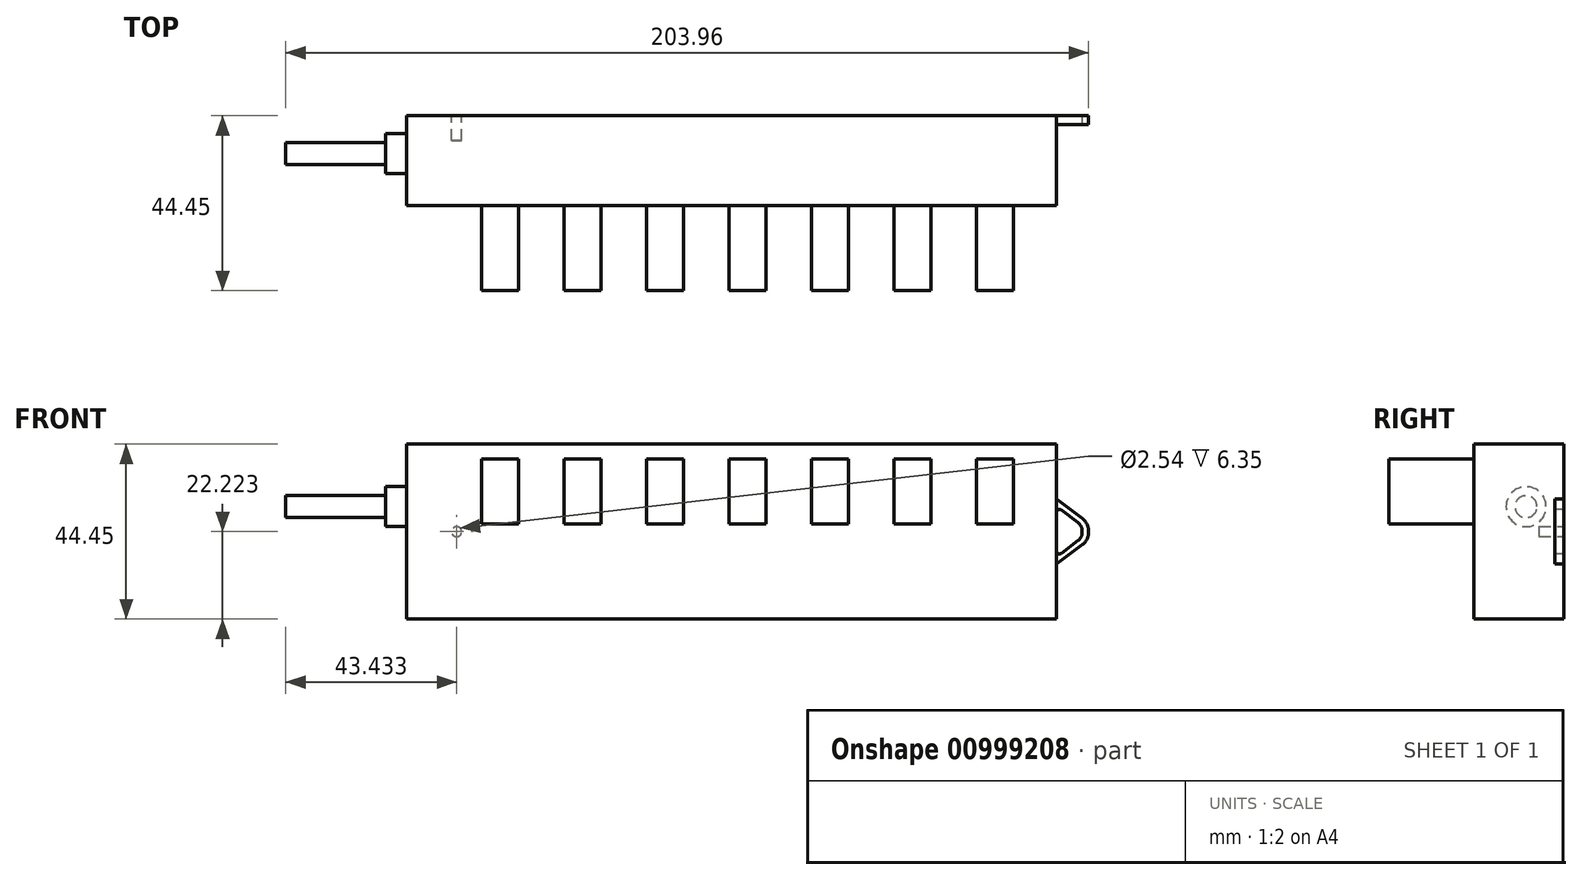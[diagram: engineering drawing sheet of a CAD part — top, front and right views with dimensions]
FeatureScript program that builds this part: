
annotation { "Feature Type Name" : "Feature", "Feature Type Description" : "" }
export const myFeature = defineFeature(function(context is Context, id is Id, definition is map)
    precondition{}
    {
        {
            var Q0;
            Q0=qCreatedBy(makeId("Front.planeOp"),FACE);
            var sketch = newSketch(context, id + "F0", { "sketchPlane" : qUnion([Q0])});
            skLineSegment(sketch, "E0.bottom", {"start": v(-60.25, 51.98) * mm, "end": v(104.85, 51.98) * mm});
            skLineSegment(sketch, "E0.top", {"start": v(-60.25, 7.53) * mm, "end": v(104.85, 7.53) * mm});
            skLineSegment(sketch, "E0.left", {"start": v(-60.25, 51.98) * mm, "end": v(-60.25, 7.53) * mm});
            skLineSegment(sketch, "E0.right", {"start": v(104.85, 51.98) * mm, "end": v(104.85, 7.53) * mm});
            skSolve(sketch);
        }
        {
            var Q0;
            Q0=makeQuery(id+"F0.imprint","IMPRINT",FACE,{"disambiguationData":[TD([[makeQuery(id+"F0.imprint","IMPRINT",EDGE,{"derivedFrom":sQuery(id+"F0.wireOp",EDGE,"E0.bottom")}),-1.0]])]});
            extrude(context, id + "F1", {"entities" : qUnion([Q0]), "depth" : 22.86 * mm, "offsetDistance" : 25.4 * mm});
        }
        {
            var Q0;
            Q0=makeQuery(id+"F1.opExtrude","SWEPT_FACE",FACE,{"disambiguationData":[OSD([sQuery(id+"F0.wireOp",EDGE,"E0.left")])]});
            var sketch = newSketch(context, id + "F2", { "sketchPlane" : qUnion([Q0])});
            skCircle(sketch, "E1", {"center": v(9.65, 36.1) * mm, "radius": 5.08 * mm});
            skSolve(sketch);
        }
        {
            var Q0;
            Q0 = qSketchRegion(id + "F2", true);
            extrude(context, id + "F3", {"entities" : qUnion([Q0]), "operationType" : NewBodyOperationType.ADD, "depth" : 5.33 * mm, "offsetDistance" : 25.4 * mm});
        }
        {
            var Q0;
            Q0=makeQuery(id+"F3.opExtrude","CAP_FACE",FACE,{"disambiguationData":[OSD([sQuery(id+"F2.wireOp",EDGE,"E1")])],"isStart":false});
            var sketch = newSketch(context, id + "F4", { "sketchPlane" : qUnion([Q0])});
            skCircle(sketch, "E2", {"center": v(9.65, 36.1) * mm, "radius": 2.8 * mm});
            skSolve(sketch);
        }
        {
            var Q0;
            Q0 = qSketchRegion(id + "F4", true);
            extrude(context, id + "F5", {"entities" : qUnion([Q0]), "operationType" : NewBodyOperationType.ADD, "depth" : 25.4 * mm, "offsetDistance" : 25.4 * mm});
        }
        {
            var Q0;
            Q0=makeQuery(id+"F1.opExtrude","CAP_FACE",FACE,{"disambiguationData":[OSD([sQuery(id+"F0.wireOp",EDGE,"E0.bottom"),sQuery(id+"F0.wireOp",EDGE,"E0.top"),sQuery(id+"F0.wireOp",EDGE,"E0.left"),sQuery(id+"F0.wireOp",EDGE,"E0.right")])],"isStart":false});
            var sketch = newSketch(context, id + "F6", { "sketchPlane" : qUnion([Q0])});
            skLineSegment(sketch, "E3.bottom", {"start": v(-41.2, 48.17) * mm, "end": v(-31.8, 48.17) * mm});
            skLineSegment(sketch, "E3.top", {"start": v(-41.2, 31.66) * mm, "end": v(-31.8, 31.66) * mm});
            skLineSegment(sketch, "E3.left", {"start": v(-41.2, 48.17) * mm, "end": v(-41.2, 31.66) * mm});
            skLineSegment(sketch, "E3.right", {"start": v(-31.8, 48.17) * mm, "end": v(-31.8, 31.66) * mm});
            skLineSegment(sketch, "E4.1.0.0", {"start": v(-10.84, 48.17) * mm, "end": v(-10.84, 31.66) * mm});
            skLineSegment(sketch, "E4.1.0.1", {"start": v(-20.24, 48.17) * mm, "end": v(-10.84, 48.17) * mm});
            skLineSegment(sketch, "E4.1.0.2", {"start": v(-20.24, 48.17) * mm, "end": v(-20.24, 31.66) * mm});
            skLineSegment(sketch, "E4.1.0.3", {"start": v(-20.24, 31.66) * mm, "end": v(-10.84, 31.66) * mm});
            skLineSegment(sketch, "E4.2.0.0", {"start": v(10.11, 48.17) * mm, "end": v(10.11, 31.66) * mm});
            skLineSegment(sketch, "E4.2.0.1", {"start": v(0.71, 48.17) * mm, "end": v(10.11, 48.17) * mm});
            skLineSegment(sketch, "E4.2.0.2", {"start": v(0.71, 48.17) * mm, "end": v(0.71, 31.66) * mm});
            skLineSegment(sketch, "E4.2.0.3", {"start": v(0.71, 31.66) * mm, "end": v(10.11, 31.66) * mm});
            skLineSegment(sketch, "E4.3.0.0", {"start": v(31.07, 48.17) * mm, "end": v(31.07, 31.66) * mm});
            skLineSegment(sketch, "E4.3.0.1", {"start": v(21.67, 48.17) * mm, "end": v(31.07, 48.17) * mm});
            skLineSegment(sketch, "E4.3.0.2", {"start": v(21.67, 48.17) * mm, "end": v(21.67, 31.66) * mm});
            skLineSegment(sketch, "E4.3.0.3", {"start": v(21.67, 31.66) * mm, "end": v(31.07, 31.66) * mm});
            skLineSegment(sketch, "E4.4.0.0", {"start": v(52.02, 48.17) * mm, "end": v(52.02, 31.66) * mm});
            skLineSegment(sketch, "E4.4.0.1", {"start": v(42.62, 48.17) * mm, "end": v(52.02, 48.17) * mm});
            skLineSegment(sketch, "E4.4.0.2", {"start": v(42.62, 48.17) * mm, "end": v(42.62, 31.66) * mm});
            skLineSegment(sketch, "E4.4.0.3", {"start": v(42.62, 31.66) * mm, "end": v(52.02, 31.66) * mm});
            skLineSegment(sketch, "E4.5.0.0", {"start": v(72.98, 48.17) * mm, "end": v(72.98, 31.66) * mm});
            skLineSegment(sketch, "E4.5.0.1", {"start": v(63.58, 48.17) * mm, "end": v(72.98, 48.17) * mm});
            skLineSegment(sketch, "E4.5.0.2", {"start": v(63.58, 48.17) * mm, "end": v(63.58, 31.66) * mm});
            skLineSegment(sketch, "E4.5.0.3", {"start": v(63.58, 31.66) * mm, "end": v(72.98, 31.66) * mm});
            skLineSegment(sketch, "E4.6.0.0", {"start": v(93.93, 48.17) * mm, "end": v(93.93, 31.66) * mm});
            skLineSegment(sketch, "E4.6.0.1", {"start": v(84.53, 48.17) * mm, "end": v(93.93, 48.17) * mm});
            skLineSegment(sketch, "E4.6.0.2", {"start": v(84.53, 48.17) * mm, "end": v(84.53, 31.66) * mm});
            skLineSegment(sketch, "E4.6.0.3", {"start": v(84.53, 31.66) * mm, "end": v(93.93, 31.66) * mm});
            skLineSegment(sketch, "E4.direction1", {"start": v(-31.8, 31.66) * mm, "end": v(-10.84, 31.66) * mm, "construction": true});
            skSolve(sketch);
        }
        {
            var Q0;
            Q0 = qSketchRegion(id + "F6", true);
            extrude(context, id + "F7", {"entities" : qUnion([Q0]), "operationType" : NewBodyOperationType.ADD, "depth" : 21.59 * mm, "offsetDistance" : 25.4 * mm});
        }
        {
            var Q0;
            Q0=makeQuery(id+"F1.opExtrude","SWEPT_FACE",FACE,{"disambiguationData":[OSD([sQuery(id+"F0.wireOp",EDGE,"E0.right")])]});
            var sketch = newSketch(context, id + "F8", { "sketchPlane" : qUnion([Q0])});
            skLineSegment(sketch, "E5.bottom", {"start": v(0, 38) * mm, "end": v(-2.29, 38) * mm});
            skLineSegment(sketch, "E5.top", {"start": v(0, 21.5) * mm, "end": v(-2.29, 21.5) * mm});
            skLineSegment(sketch, "E5.left", {"start": v(0, 38) * mm, "end": v(0, 21.5) * mm});
            skLineSegment(sketch, "E5.right", {"start": v(-2.29, 38) * mm, "end": v(-2.29, 21.5) * mm});
            skSolve(sketch);
        }
        {
            var Q0;
            Q0 = qSketchRegion(id + "F8", true);
            extrude(context, id + "F9", {"entities" : qUnion([Q0]), "operationType" : NewBodyOperationType.ADD, "depth" : 8.13 * mm, "offsetDistance" : 25.4 * mm});
        }
        {
            var Q0;
            Q0=makeQuery(id+"F9.opExtrude","SWEPT_FACE",FACE,{"disambiguationData":[OSD([sQuery(id+"F8.wireOp",EDGE,"E5.right")])]});
            var sketch = newSketch(context, id + "F10", { "sketchPlane" : qUnion([Q0])});
            skLineSegment(sketch, "E6", {"start": v(104.85, 38) * mm, "end": v(111.46, 33.06) * mm});
            skLineSegment(sketch, "E7", {"start": v(104.85, 38) * mm, "end": v(112.98, 38) * mm});
            skLineSegment(sketch, "E8", {"start": v(112.98, 38) * mm, "end": v(112.98, 31.91) * mm});
            skLineSegment(sketch, "E9", {"start": v(104.85, 29.75) * mm, "end": v(112.98, 29.75) * mm, "construction": true});
            skLineSegment(sketch, "E10", {"start": v(106.07, 35.24) * mm, "end": v(110.34, 32.04) * mm});
            skLineSegment(sketch, "E11", {"start": v(111.36, 30) * mm, "end": v(111.36, 29.75) * mm});
            skPoint(sketch, "E12.visualSharp", {"position": v(111.36, 31.28) * mm});
            skArc(sketch, "E12.filletArc", {"start": v(111.36, 30) * mm, "mid": v(111.09, 31.14) * mm, "end": v(110.34, 32.04) * mm});
            skLineSegment(sketch, "E13", {"start": v(112.98, 30) * mm, "end": v(112.98, 29.75) * mm});
            skPoint(sketch, "E14.visualSharp", {"position": v(112.98, 31.91) * mm});
            skArc(sketch, "E14.filletArc", {"start": v(112.98, 30) * mm, "mid": v(112.58, 31.71) * mm, "end": v(111.46, 33.06) * mm});
            skLineSegment(sketch, "E15", {"start": v(104.85, 34.63) * mm, "end": v(104.85, 29.75) * mm});
            skPoint(sketch, "E16.visualSharp", {"position": v(104.85, 36.15) * mm});
            skArc(sketch, "E16.filletArc", {"start": v(106.07, 35.24) * mm, "mid": v(105.27, 35.31) * mm, "end": v(104.85, 34.63) * mm});
            skLineSegment(sketch, "E17", {"start": v(111.36, 29.75) * mm, "end": v(104.85, 29.75) * mm});
            skLineSegment(sketch, "E18", {"start": v(112.98, 31.91) * mm, "end": v(112.98, 29.75) * mm});
            skLineSegment(sketch, "E19.MirrorCS", {"start": v(104.85, 24.88) * mm, "end": v(104.85, 29.75) * mm});
            skArc(sketch, "E20.MirrorCS", {"start": v(106.07, 24.27) * mm, "mid": v(105.27, 24.2) * mm, "end": v(104.85, 24.88) * mm});
            skLineSegment(sketch, "E21.MirrorCS", {"start": v(106.07, 24.27) * mm, "end": v(110.34, 27.47) * mm});
            skArc(sketch, "E22.MirrorCS", {"start": v(111.36, 29.5) * mm, "mid": v(111.09, 28.36) * mm, "end": v(110.34, 27.47) * mm});
            skLineSegment(sketch, "E23.MirrorCS", {"start": v(111.36, 29.5) * mm, "end": v(111.36, 29.75) * mm});
            skLineSegment(sketch, "E24.MirrorCS", {"start": v(112.98, 29.5) * mm, "end": v(112.98, 29.75) * mm});
            skArc(sketch, "E25.MirrorCS", {"start": v(112.98, 29.5) * mm, "mid": v(112.58, 27.8) * mm, "end": v(111.46, 26.45) * mm});
            skLineSegment(sketch, "E26.MirrorCS", {"start": v(104.85, 21.5) * mm, "end": v(111.46, 26.45) * mm});
            skLineSegment(sketch, "E27.MirrorCS", {"start": v(104.85, 21.5) * mm, "end": v(112.98, 21.5) * mm});
            skLineSegment(sketch, "E28.MirrorCS", {"start": v(112.98, 21.5) * mm, "end": v(112.98, 27.6) * mm});
            skLineSegment(sketch, "E29.MirrorCS", {"start": v(112.98, 27.6) * mm, "end": v(112.98, 29.75) * mm});
            skSolve(sketch);
        }
        {
            var Q0;
            Q0 = qSketchRegion(id + "F10", true);
            extrude(context, id + "F11", {"entities" : qUnion([Q0]), "operationType" : NewBodyOperationType.REMOVE, "oppositeDirection" : true, "depth" : 25.4 * mm, "offsetDistance" : 25.4 * mm});
        }
        {
            var Q0;
            Q0=makeQuery(id+"F9.boolean.opBoolean","MERGE",FACE,{"derivedFrom":[makeQuery(id+"F1.opExtrude","CAP_FACE",FACE,{"disambiguationData":[OSD([sQuery(id+"F0.wireOp",EDGE,"E0.bottom"),sQuery(id+"F0.wireOp",EDGE,"E0.top"),sQuery(id+"F0.wireOp",EDGE,"E0.left"),sQuery(id+"F0.wireOp",EDGE,"E0.right")])],"isStart":true}),makeQuery(id+"F9.opExtrude","SWEPT_FACE",FACE,{"disambiguationData":[OSD([sQuery(id+"F8.wireOp",EDGE,"E5.left")])]})]});
            var sketch = newSketch(context, id + "F12", { "sketchPlane" : qUnion([Q0])});
            skCircle(sketch, "E30", {"center": v(47.55, 29.75) * mm, "radius": 1.27 * mm});
            skSolve(sketch);
        }
        {
            var Q0;
            Q0 = qSketchRegion(id + "F12", true);
            extrude(context, id + "F13", {"entities" : qUnion([Q0]), "operationType" : NewBodyOperationType.REMOVE, "oppositeDirection" : true, "depth" : 6.35 * mm, "offsetDistance" : 25.4 * mm});
        }
    });
